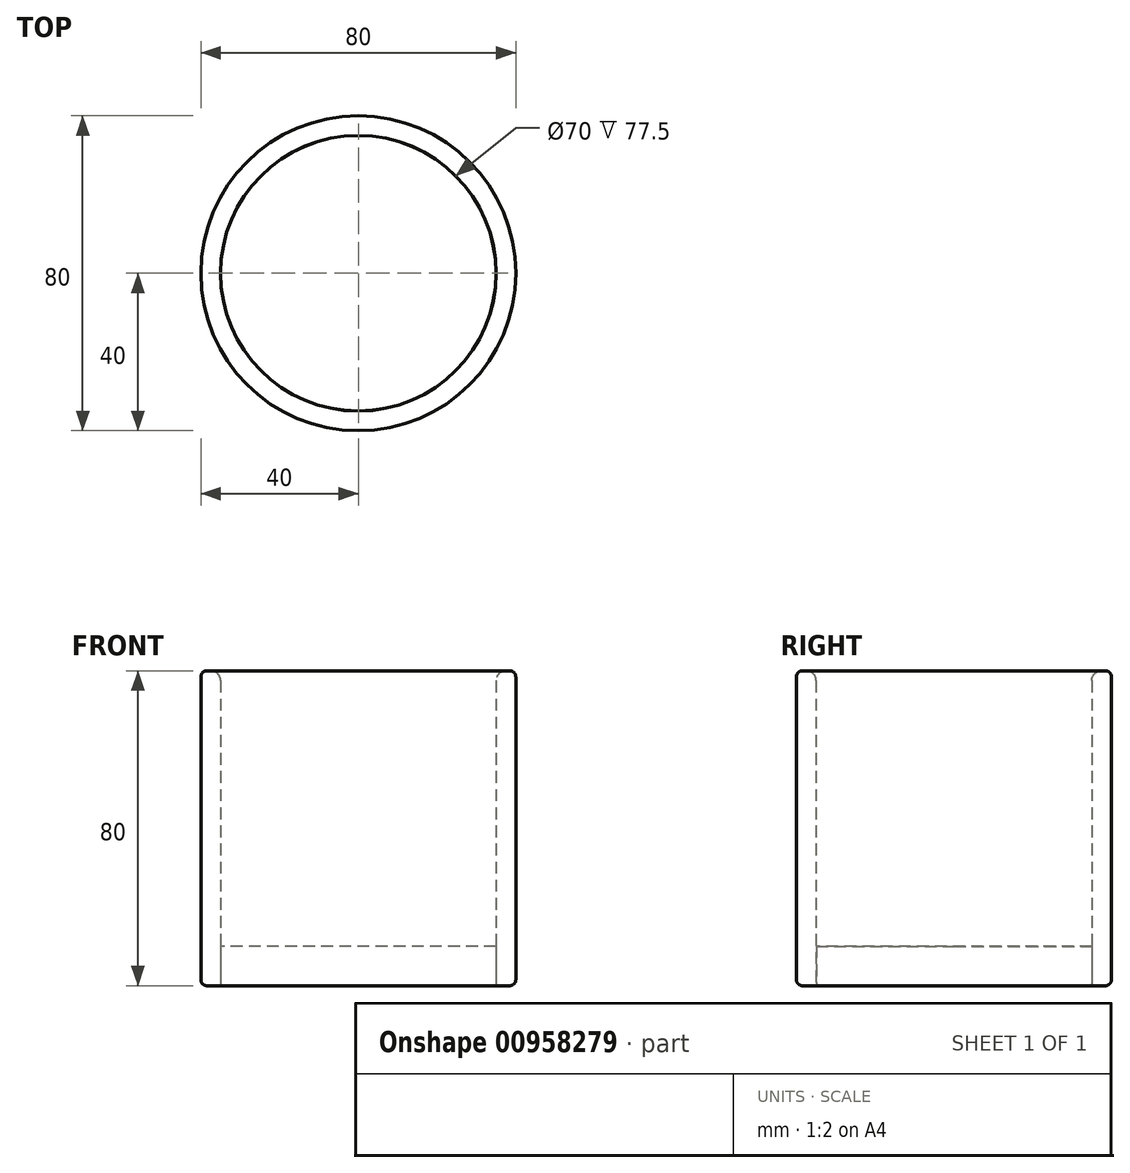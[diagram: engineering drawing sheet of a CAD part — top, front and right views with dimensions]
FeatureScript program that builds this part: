
annotation { "Feature Type Name" : "Feature", "Feature Type Description" : "" }
export const myFeature = defineFeature(function(context is Context, id is Id, definition is map)
    precondition{}
    {
        {
            var Q0;
            Q0=qCreatedBy(makeId("Top.planeOp"),FACE);
            var sketch = newSketch(context, id + "F0", { "sketchPlane" : qUnion([Q0])});
            skCircle(sketch, "E0", {"center": v(0, 0) * mm, "radius": 40 * mm});
            skCircle(sketch, "E1", {"center": v(0, 0) * mm, "radius": 35 * mm});
            skCircle(sketch, "E2", {"center": v(0, 0) * mm, "radius": 34.99 * mm});
            skSolve(sketch);
        }
        {
            var Q0;
            Q0 = qSketchRegion(id + "F0", true);
            extrude(context, id + "F1", {"entities" : qUnion([Q0]), "depth" : 80 * mm, "offsetDistance" : 25 * mm});
        }
        {
            var Q0;
            Q0=makeQuery(id+"F0.imprint","IMPRINT",FACE,{"disambiguationData":[TD([[makeQuery(id+"F0.imprint","IMPRINT",EDGE,{"derivedFrom":sQuery(id+"F0.wireOp",EDGE,"E2")}),1.0]])]});
            extrude(context, id + "F2", {"entities" : qUnion([Q0]), "depth" : 10 * mm, "offsetDistance" : 25 * mm});
        }
        {
            var Q0;
            Q0=makeQuery(id+"F1.opExtrude","CAP_EDGE",EDGE,{"disambiguationData":[OSD([sQuery(id+"F0.wireOp",EDGE,"E1")])],"isStart":false});
            fillet(context, id + "F3", {"entities" : qUnion([Q0]), "radius" : 2.5 * mm, "tangentPropagation" : true, "allowEdgeOverflow" : false});
        }
        {
            var Q0;
            Q0=makeQuery(id+"F1.opExtrude","CAP_EDGE",EDGE,{"disambiguationData":[OSD([sQuery(id+"F0.wireOp",EDGE,"E0")])],"isStart":false});
            fillet(context, id + "F4", {"entities" : qUnion([Q0]), "radius" : 1.5 * mm, "tangentPropagation" : true, "allowEdgeOverflow" : false});
        }
        {
            var Q0;
            Q0=makeQuery(id+"F2.opExtrude","CAP_FACE",FACE,{"disambiguationData":[OSD([sQuery(id+"F0.wireOp",EDGE,"E2")])],"isStart":true});
            fillet(context, id + "F5", {"entities" : qUnion([Q0]), "radius" : 0.5 * mm, "tangentPropagation" : true, "rho" : 0.5, "crossSection" : FilletCrossSection.CONIC, "allowEdgeOverflow" : false});
        }
        {
            var Q0;
            Q0=makeQuery(id+"F1.opExtrude","CAP_EDGE",EDGE,{"disambiguationData":[OSD([sQuery(id+"F0.wireOp",EDGE,"E0")])],"isStart":true});
            fillet(context, id + "F6", {"entities" : qUnion([Q0]), "radius" : 1.5 * mm, "tangentPropagation" : true, "allowEdgeOverflow" : false});
        }
    });
